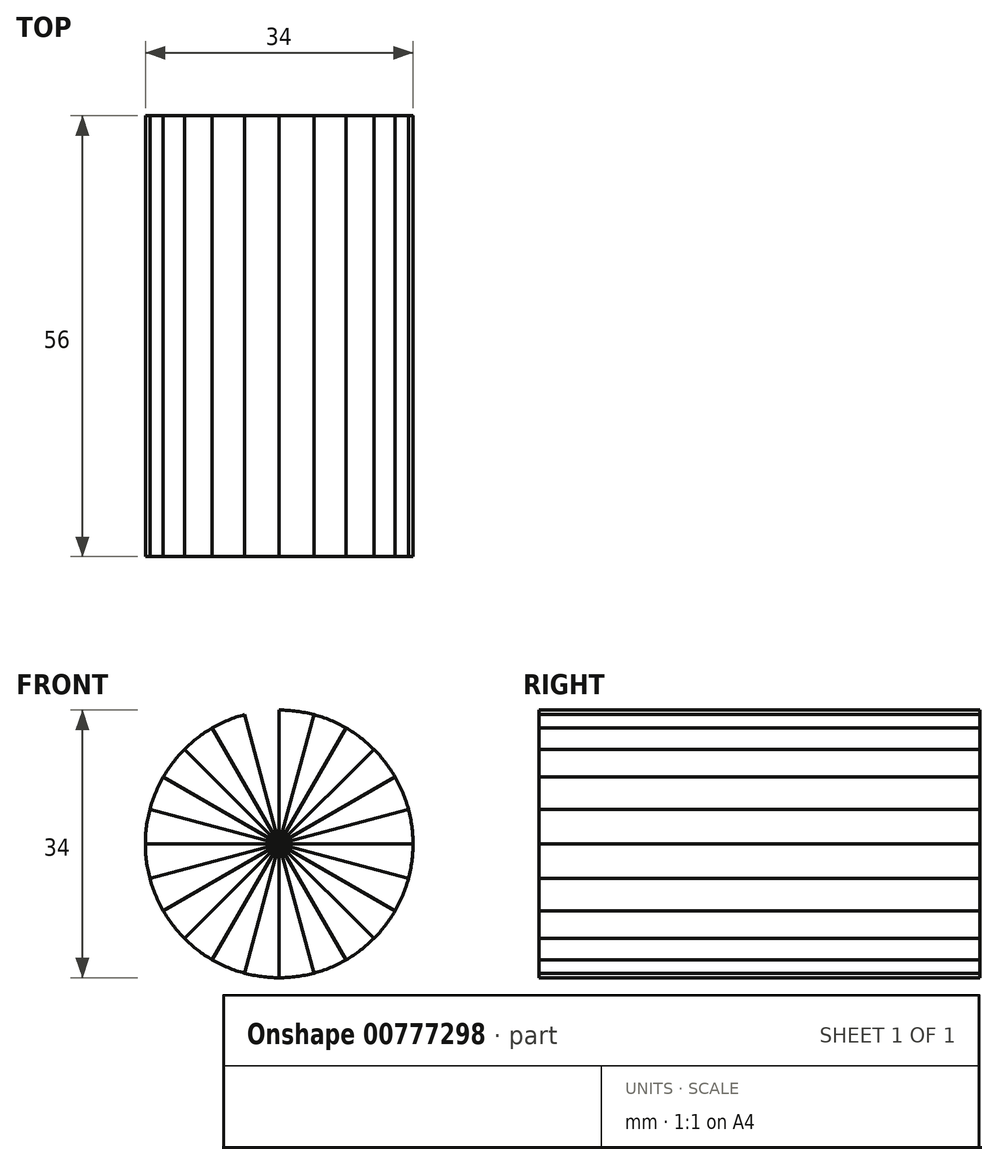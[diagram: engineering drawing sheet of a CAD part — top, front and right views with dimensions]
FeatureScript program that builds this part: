
annotation { "Feature Type Name" : "Feature", "Feature Type Description" : "" }
export const myFeature = defineFeature(function(context is Context, id is Id, definition is map)
    precondition{}
    {
        {
            var Q0;
            Q0=qCreatedBy(makeId("Front.planeOp"),FACE);
            var sketch = newSketch(context, id + "F0", { "sketchPlane" : qUnion([Q0])});
            skCircle(sketch, "E0", {"center": v(0, 0) * mm, "radius": 17 * mm});
            skLineSegment(sketch, "E1", {"start": v(0, 0) * mm, "end": v(0, 0) * mm});
            skLineSegment(sketch, "E2.MirrorCS", {"start": v(-63, 0) * mm, "end": v(-17, 0) * mm});
            skLineSegment(sketch, "E3.MirrorCS", {"start": v(-61, 5.5) * mm, "end": v(-30.77, 1.49) * mm});
            skLineSegment(sketch, "E4.MirrorCS", {"start": v(-61, -5.5) * mm, "end": v(-30.77, -1.49) * mm});
            skArc(sketch, "E5.MirrorCS", {"start": v(-30.77, 1.49) * mm, "mid": v(-29.47, 0) * mm, "end": v(-30.77, -1.49) * mm});
            skLineSegment(sketch, "E6.MirrorCS", {"start": v(-61, 1.38) * mm, "end": v(-61, 5.5) * mm});
            skLineSegment(sketch, "E7.MirrorCS", {"start": v(-63, 1.38) * mm, "end": v(-61, 1.38) * mm});
            skLineSegment(sketch, "E8.MirrorCS", {"start": v(-63, -1.38) * mm, "end": v(-61, -1.38) * mm});
            skLineSegment(sketch, "E9.MirrorCS", {"start": v(-61, -1.38) * mm, "end": v(-61, -5.5) * mm});
            skText(sketch, "E10", { "text": "correct", "fontName": "OpenSans-Regular.ttf"});
            skLineSegment(sketch, "E11.trimOffspring", {"start": v(-17, 0) * mm, "end": v(-26.3, 0) * mm});
            skLineSegment(sketch, "E12", {"start": v(0, 0) * mm, "end": v(54.99, 0) * mm});
            skLineSegment(sketch, "E13.MirrorCS", {"start": v(60.3, 9.33) * mm, "end": v(59.78, 13.26) * mm});
            skLineSegment(sketch, "E14.MirrorCS", {"start": v(60.66, 6.6) * mm, "end": v(61.17, 2.66) * mm});
            skLineSegment(sketch, "E15.MirrorCS", {"start": v(61.17, 2.66) * mm, "end": v(30.7, 2.54) * mm});
            skLineSegment(sketch, "E16.MirrorCS", {"start": v(59.78, 13.26) * mm, "end": v(30.32, 5.5) * mm});
            skArc(sketch, "E17.MirrorCS", {"start": v(30.32, 5.5) * mm, "mid": v(29.22, 3.85) * mm, "end": v(30.7, 2.54) * mm});
            skLineSegment(sketch, "E18.MirrorCS", {"start": v(62.46, 8.23) * mm, "end": v(0, 0) * mm});
            skLineSegment(sketch, "E19.MirrorCS", {"start": v(62.28, 9.6) * mm, "end": v(62.64, 6.86) * mm});
            skLineSegment(sketch, "E20.MirrorCS", {"start": v(62.64, 6.86) * mm, "end": v(60.66, 6.6) * mm});
            skLineSegment(sketch, "E21.MirrorCS", {"start": v(62.28, 9.6) * mm, "end": v(60.3, 9.33) * mm});
            skLineSegment(sketch, "E22.MirrorCS", {"start": v(1.38, 59) * mm, "end": v(5.34, 59) * mm});
            skLineSegment(sketch, "E23.MirrorCS", {"start": v(-1.38, 59) * mm, "end": v(-5.35, 59) * mm});
            skLineSegment(sketch, "E24.MirrorCS", {"start": v(-1.38, 61) * mm, "end": v(-1.38, 59) * mm});
            skLineSegment(sketch, "E25.MirrorCS", {"start": v(1.38, 61) * mm, "end": v(1.38, 59) * mm});
            skLineSegment(sketch, "E26", {"start": v(0, 29.47) * mm, "end": v(0, 0) * mm});
            skLineSegment(sketch, "E27", {"start": v(0, 29.47) * mm, "end": v(0, 63.31) * mm, "construction": true});
            skLineSegment(sketch, "E28", {"start": v(5.34, 59) * mm, "end": v(1.63, 30.83) * mm});
            skLineSegment(sketch, "E29.MirrorCS", {"start": v(-5.34, 59) * mm, "end": v(-1.63, 30.83) * mm});
            skArc(sketch, "E30", {"start": v(-1.63, 30.83) * mm, "mid": v(0, 29.47) * mm, "end": v(1.63, 30.83) * mm});
            skLineSegment(sketch, "E31", {"start": v(0, 0) * mm, "end": v(-7.67, 58.28) * mm});
            skLineSegment(sketch, "E32.MirrorCS", {"start": v(-10.1, 58.37) * mm, "end": v(-6.4, 30.2) * mm});
            skLineSegment(sketch, "E33.MirrorCS", {"start": v(-7.62, 28.47) * mm, "end": v(0, 0) * mm});
            skArc(sketch, "E34.MirrorCS", {"start": v(-6.4, 30.2) * mm, "mid": v(-7.62, 28.47) * mm, "end": v(-9.55, 29.36) * mm});
            skLineSegment(sketch, "E35.MirrorCS", {"start": v(-7.62, 28.47) * mm, "end": v(-16.38, 61.16) * mm, "construction": true});
            skLineSegment(sketch, "E36.MirrorCS", {"start": v(-20.43, 55.6) * mm, "end": v(-9.55, 29.36) * mm});
            skLineSegment(sketch, "E37.MirrorCS", {"start": v(-14.45, 59.28) * mm, "end": v(-13.93, 57.35) * mm});
            skLineSegment(sketch, "E38.MirrorCS", {"start": v(-17.11, 58.57) * mm, "end": v(-16.6, 56.63) * mm});
            skLineSegment(sketch, "E39.MirrorCS", {"start": v(-13.93, 57.35) * mm, "end": v(-10.1, 58.37) * mm});
            skLineSegment(sketch, "E40.MirrorCS", {"start": v(-16.6, 56.63) * mm, "end": v(-20.43, 55.6) * mm});
            skArc(sketch, "E41", {"start": v(-14.45, 59.28) * mm, "mid": v(-7.96, 60.5) * mm, "end": v(-1.38, 61) * mm});
            skPoint(sketch, "E42.startSnap0", {"position": v(0, 46.4) * mm});
            const initialGuessF0  = {"E10": [-0.06317, -0.01425, 1, 0, 0.0042]};
            skSetInitialGuess(sketch, initialGuessF0);
            skSolve(sketch);
        }
        {
            var Q0;
            {var subQ0=sQuery(id+"F0.wireOp",EDGE,"89b28252-0f95-40a1-8d6f-cb6967cd3bbc0.MirrorCS");var subQ1=sQuery(id+"F0.wireOp",EDGE,"527cb00f-083c-40bb-afd1-fc9c13b6854b0.MirrorC");var subQ2=makeQuery(id+"F0.imprint","INTERSECT",VERTEX,{"derivedFrom":[subQ1,subQ0]});Q0=makeQuery(id+"F0.imprint","IMPRINT",FACE,{"disambiguationData":[TD([[makeQuery(id+"F0.imprint","IMPRINT",EDGE,{"disambiguationData":[TD([[subQ2,-1.0]])],"derivedFrom":subQ1}),-1.0]])]});}
            var Q1;
            {var subQ0=sQuery(id+"F0.wireOp",EDGE,"0eea7ff2-b1bc-485e-ab4f-c961036434e3");var subQ1=sQuery(id+"F0.wireOp",EDGE,"527cb00f-083c-40bb-afd1-fc9c13b6854b0.MirrorC");var subQ2=makeQuery(id+"F0.imprint","INTERSECT",VERTEX,{"derivedFrom":[subQ1,subQ0]});Q1=makeQuery(id+"F0.imprint","IMPRINT",FACE,{"disambiguationData":[TD([[makeQuery(id+"F0.imprint","IMPRINT",EDGE,{"disambiguationData":[TD([[subQ2,-1.0]])],"derivedFrom":subQ1}),-1.0]])]});}
            var Q2;
            {var subQ0=sQuery(id+"F0.wireOp",EDGE,"E18.MirrorCS");var subQ1=sQuery(id+"F0.wireOp",EDGE,"527cb00f-083c-40bb-afd1-fc9c13b6854b0.MirrorC");var subQ2=makeQuery(id+"F0.imprint","INTERSECT",VERTEX,{"derivedFrom":[subQ1,subQ0]});Q2=makeQuery(id+"F0.imprint","IMPRINT",FACE,{"disambiguationData":[TD([[makeQuery(id+"F0.imprint","IMPRINT",EDGE,{"disambiguationData":[TD([[subQ2,-1.0]])],"derivedFrom":subQ1}),-1.0]])]});}
            var Q3;
            {var subQ0=sQuery(id+"F0.wireOp",EDGE,"3ad31dce-3ccf-47e7-8061-e2701dc9b31b0.MirrorCS");var subQ1=sQuery(id+"F0.wireOp",EDGE,"527cb00f-083c-40bb-afd1-fc9c13b6854b0.MirrorC");var subQ2=makeQuery(id+"F0.imprint","INTERSECT",VERTEX,{"derivedFrom":[subQ1,subQ0]});Q3=makeQuery(id+"F0.imprint","IMPRINT",FACE,{"disambiguationData":[TD([[makeQuery(id+"F0.imprint","IMPRINT",EDGE,{"disambiguationData":[TD([[subQ2,-1.0]])],"derivedFrom":subQ1}),-1.0]])]});}
            var Q4;
            {var subQ1=sQuery(id+"F0.wireOp",EDGE,"E0");var subQ5=makeQuery(id+"F0.imprint","INTERSECT",VERTEX,{"derivedFrom":[subQ1,sQuery(id+"F0.wireOp",EDGE,"E11.trimOffspring")]});Q4=makeQuery(id+"F0.imprint","IMPRINT",FACE,{"disambiguationData":[TD([[makeQuery(id+"F0.imprint","IMPRINT",EDGE,{"disambiguationData":[TD([[subQ5,1.0]])],"derivedFrom":subQ1}),1.0]])]});}
            var Q5;
            {var subQ7=sQuery(id+"F0.wireOp",EDGE,"239feb4f-5ad5-4651-a374-b5203ac474610.MirrorCS");Q5=makeQuery(id+"F0.imprint","IMPRINT",FACE,{"disambiguationData":[TD([[makeQuery(id+"F0.imprint","IMPRINT",EDGE,{"derivedFrom":subQ7}),1.0]])]});}
            extrude(context, id + "F1", {"entities" : qUnion([Q0, Q1, Q2, Q3, Q4, Q5]), "depth" : 56 * mm, "offsetDistance" : 25 * mm});
        }
        {
            var Q0;
            Q0=makeQuery(id+"F1.opExtrude","SWEPT_BODY",BODY,{"disambiguationData":[OSD([sQuery(id+"F0.wireOp",EDGE,"E0"),sQuery(id+"F0.wireOp",EDGE,"3ad31dce-3ccf-47e7-8061-e2701dc9b31b0.MirrorCS"),sQuery(id+"F0.wireOp",EDGE,"71db1e61-7082-4584-82c3-abd0c18eec3b0.MirrorCS"),sQuery(id+"F0.wireOp",EDGE,"239feb4f-5ad5-4651-a374-b5203ac474610.MirrorCS"),sQuery(id+"F0.wireOp",EDGE,"e93d65c6-07ac-49f3-ad26-1a83865d423b0.MirrorCS"),sQuery(id+"F0.wireOp",EDGE,"84c01898-2c53-4909-8250-393accea20b90.MirrorCS"),sQuery(id+"F0.wireOp",EDGE,"ebab1920-626e-47f6-88e6-0858ccfd16280.MirrorCS"),sQuery(id+"F0.wireOp",EDGE,"15ef508f-5264-4afd-8862-2d921255fcc40.MirrorCS"),sQuery(id+"F0.wireOp",EDGE,"89b28252-0f95-40a1-8d6f-cb6967cd3bbc0.MirrorCS"),sQuery(id+"F0.wireOp",EDGE,"fcb4bb2b-a0aa-4b66-8de0-3ded20cb11ca0.MirrorCS"),sQuery(id+"F0.wireOp",EDGE,"9f3b9d48-d622-403f-8c87-8de4a1e6c6170.MirrorCS"),sQuery(id+"F0.wireOp",EDGE,"7488719c-1d5b-4a0d-b1b8-cb229dd97080")])]});
            var Q1;
            {var subQ0=sQuery(id+"F0.wireOp",EDGE,"E0");var subQ1=makeQuery(id+"F0.imprint","INTERSECT",VERTEX,{"derivedFrom":[subQ0,sQuery(id+"F0.wireOp",EDGE,"E11.trimOffspring")]});Q1=makeQuery(id+"F1.opExtrude","SWEPT_FACE",FACE,{"disambiguationData":[OSD([subQ0]),TDD([makeQuery(id+"F0.imprint","IMPRINT",EDGE,{"disambiguationData":[TD([[subQ1,1.0]])],"derivedFrom":subQ0}),makeQuery(id+"F0.imprint","IMPRINT",EDGE,{"disambiguationData":[TD([[subQ1,-1.0]])],"derivedFrom":subQ0})])]});}
            circularPattern(context, id + "F2", {"entities" : qUnion([Q0]), "axis" : qUnion([Q1]), "angle" : 360 * degree, "instanceCount" : 24, "equalSpace" : true});
        }
        {
            var Q0;
            {var subQ1=sQuery(id+"F0.wireOp",EDGE,"E0");var subQ5=makeQuery(id+"F0.imprint","INTERSECT",VERTEX,{"derivedFrom":[subQ1,sQuery(id+"F0.wireOp",EDGE,"E11.trimOffspring")]});Q0=makeQuery(id+"F0.imprint","IMPRINT",FACE,{"disambiguationData":[TD([[makeQuery(id+"F0.imprint","IMPRINT",EDGE,{"disambiguationData":[TD([[subQ5,1.0]])],"derivedFrom":subQ1}),1.0]])]});}
            var Q1;
            {var subQ0=sQuery(id+"F0.wireOp",EDGE,"89b28252-0f95-40a1-8d6f-cb6967cd3bbc0.MirrorCS");var subQ1=sQuery(id+"F0.wireOp",EDGE,"527cb00f-083c-40bb-afd1-fc9c13b6854b0.MirrorC");var subQ2=makeQuery(id+"F0.imprint","INTERSECT",VERTEX,{"derivedFrom":[subQ1,subQ0]});Q1=makeQuery(id+"F0.imprint","IMPRINT",FACE,{"disambiguationData":[TD([[makeQuery(id+"F0.imprint","IMPRINT",EDGE,{"disambiguationData":[TD([[subQ2,-1.0]])],"derivedFrom":subQ1}),-1.0]])]});}
            var Q2;
            {var subQ0=sQuery(id+"F0.wireOp",EDGE,"0eea7ff2-b1bc-485e-ab4f-c961036434e3");var subQ1=sQuery(id+"F0.wireOp",EDGE,"527cb00f-083c-40bb-afd1-fc9c13b6854b0.MirrorC");var subQ2=makeQuery(id+"F0.imprint","INTERSECT",VERTEX,{"derivedFrom":[subQ1,subQ0]});Q2=makeQuery(id+"F0.imprint","IMPRINT",FACE,{"disambiguationData":[TD([[makeQuery(id+"F0.imprint","IMPRINT",EDGE,{"disambiguationData":[TD([[subQ2,-1.0]])],"derivedFrom":subQ1}),-1.0]])]});}
            var Q3;
            {var subQ0=sQuery(id+"F0.wireOp",EDGE,"3ad31dce-3ccf-47e7-8061-e2701dc9b31b0.MirrorCS");var subQ1=sQuery(id+"F0.wireOp",EDGE,"527cb00f-083c-40bb-afd1-fc9c13b6854b0.MirrorC");var subQ2=makeQuery(id+"F0.imprint","INTERSECT",VERTEX,{"derivedFrom":[subQ1,subQ0]});Q3=makeQuery(id+"F0.imprint","IMPRINT",FACE,{"disambiguationData":[TD([[makeQuery(id+"F0.imprint","IMPRINT",EDGE,{"disambiguationData":[TD([[subQ2,-1.0]])],"derivedFrom":subQ1}),-1.0]])]});}
            var Q4;
            {var subQ0=sQuery(id+"F0.wireOp",EDGE,"E18.MirrorCS");var subQ1=sQuery(id+"F0.wireOp",EDGE,"527cb00f-083c-40bb-afd1-fc9c13b6854b0.MirrorC");var subQ2=makeQuery(id+"F0.imprint","INTERSECT",VERTEX,{"derivedFrom":[subQ1,subQ0]});Q4=makeQuery(id+"F0.imprint","IMPRINT",FACE,{"disambiguationData":[TD([[makeQuery(id+"F0.imprint","IMPRINT",EDGE,{"disambiguationData":[TD([[subQ2,-1.0]])],"derivedFrom":subQ1}),-1.0]])]});}
            extrude(context, id + "F3", {"entities" : qUnion([Q0, Q1, Q2, Q3, Q4]), "operationType" : NewBodyOperationType.REMOVE, "depth" : 56 * mm, "offsetDistance" : 25 * mm});
        }
    });
